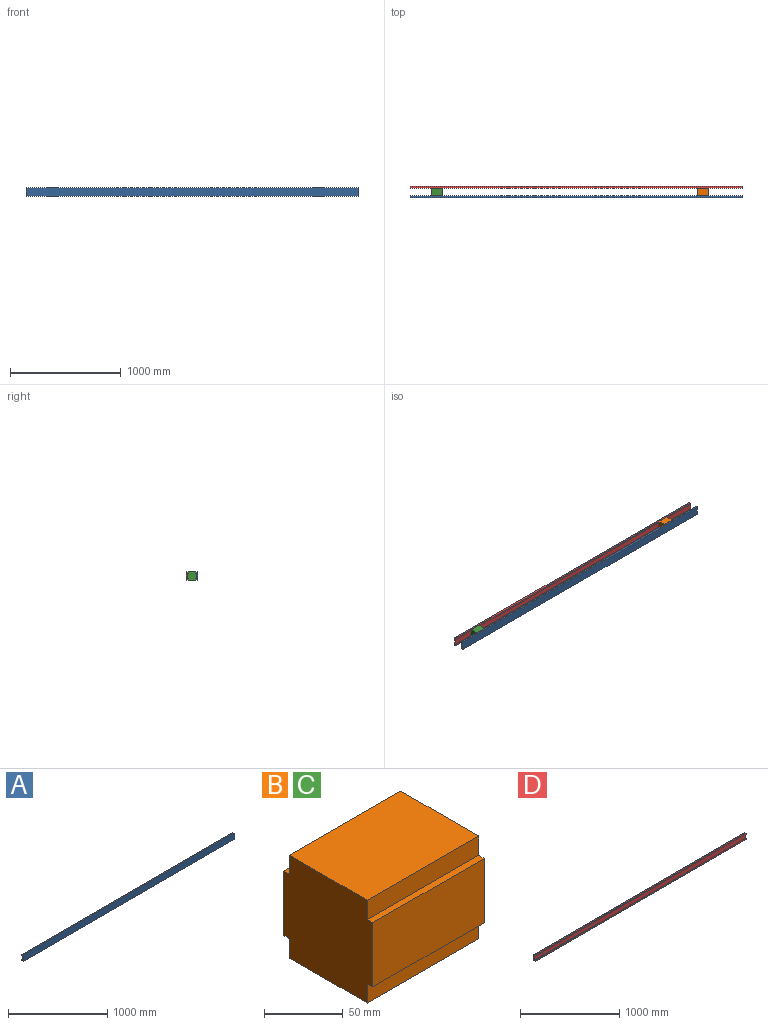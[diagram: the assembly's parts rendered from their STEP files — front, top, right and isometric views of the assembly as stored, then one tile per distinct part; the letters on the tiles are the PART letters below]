
ASSEMBLY  parts=4 mates=6
PART A: 10 faces, bbox 3000x15x80 mm
  f0: plane 3000x80mm, normal (0,-1,0), area 240000mm2, adj f1,f7,f8,f9
  f1: plane 3000x15mm, normal (0,0,-1), area 45000mm2, adj f0,f2,f8,f9
  f2: plane 3000x15mm, normal (0,1,0), area 45000mm2, adj f1,f3,f8,f9
  f3: plane 3000x5mm, normal (0,0,1), area 15000mm2, adj f2,f4,f8,f9
  f4: plane 3000x50mm, normal (0,1,0), area 150000mm2, adj f3,f5,f8,f9
  f5: plane 3000x5mm, normal (0,0,-1), area 15000mm2, adj f4,f6,f8,f9
  f6: plane 3000x15mm, normal (0,1,0), area 45000mm2, adj f5,f7,f8,f9
  f7: plane 3000x15mm, normal (0,0,1), area 45000mm2, adj f0,f6,f8,f9
  f8: plane 80x15mm, normal (1,0,0), area 950mm2, adj f0,f1,f2,f3,f4,f5,f6,f7
  f9: plane 80x15mm, normal (-1,0,0), area 950mm2, adj f0,f1,f2,f3,f4,f5,f6,f7
PART B: 14 faces, bbox 100x80x80 mm
  f0: plane 100x5mm, normal (0,0,1), area 500mm2, adj f1,f11,f12,f13
  f1: plane 100x15mm, normal (0,1,0), area 1500mm2, adj f0,f2,f12,f13
  f2: plane 100x70mm, normal (0,0,1), area 7000mm2, adj f1,f3,f12,f13
  f3: plane 100x15mm, normal (0,-1,0), area 1500mm2, adj f2,f4,f12,f13
  f4: plane 100x5mm, normal (0,0,1), area 500mm2, adj f3,f5,f12,f13
  f5: plane 100x50mm, normal (0,-1,0), area 5000mm2, adj f4,f6,f12,f13
  f6: plane 100x5mm, normal (0,0,-1), area 500mm2, adj f5,f7,f12,f13
  f7: plane 100x15mm, normal (0,-1,0), area 1500mm2, adj f6,f8,f12,f13
  f8: plane 100x70mm, normal (0,0,-1), area 7000mm2, adj f7,f9,f12,f13
  f9: plane 100x15mm, normal (0,1,0), area 1500mm2, adj f8,f10,f12,f13
  f10: plane 100x5mm, normal (0,0,-1), area 500mm2, adj f9,f11,f12,f13
  f11: plane 100x50mm, normal (0,1,0), area 5000mm2, adj f0,f10,f12,f13
  f12: plane 80x80mm, normal (1,0,0), area 6100mm2, adj f0,f1,f2,f3,f4,f5,f6,f7
  f13: plane 80x80mm, normal (-1,0,0), area 6100mm2, adj f0,f1,f2,f3,f4,f5,f6,f7
PART C: same geometry as B
PART D: 10 faces, bbox 3000x15x80 mm
  f0: plane 3000x15mm, normal (0,-1,0), area 45000mm2, adj f1,f7,f8,f9
  f1: plane 3000x15mm, normal (0,0,-1), area 45000mm2, adj f0,f2,f8,f9
  f2: plane 3000x80mm, normal (0,1,0), area 240000mm2, adj f1,f3,f8,f9
  f3: plane 3000x15mm, normal (0,0,1), area 45000mm2, adj f2,f4,f8,f9
  f4: plane 3000x15mm, normal (0,-1,0), area 45000mm2, adj f3,f5,f8,f9
  f5: plane 3000x5mm, normal (0,0,-1), area 15000mm2, adj f4,f6,f8,f9
  f6: plane 3000x50mm, normal (0,-1,0), area 150000mm2, adj f5,f7,f8,f9
  f7: plane 3000x5mm, normal (0,0,1), area 15000mm2, adj f0,f6,f8,f9
  f8: plane 80x15mm, normal (1,0,0), area 950mm2, adj f0,f1,f2,f3,f4,f5,f6,f7
  f9: plane 80x15mm, normal (-1,0,0), area 950mm2, adj f0,f1,f2,f3,f4,f5,f6,f7
PLACE A t=(-1500,-100,-80)mm
PLACE B t=(-355.96,-100,-80)mm
PLACE C t=(-2752.44,-100,-80)mm
PLACE D t=(-1500,-100,-80)mm
MATE parallel D.f2 <-> A.f0  axis (0,1,0) through (-3000,0,-40)mm
MATE slider B.f13 <-> A.f9  axis (-1,0,0) through (-405.96,-85,-15)mm
MATE planar D.f3 <-> A.f7  axis (0,0,1) through (-1500,-7.5,0)mm
MATE planar A.f9 <-> D.f9  axis (-1,0,0) through (-3000,-92.5,0)mm
MATE slider C.f13 <-> D.f9  axis (-1,0,0) through (-2802.44,-15,-15)mm
MATE slider B.f13 <-> D.f9  axis (-1,0,0) through (-405.96,-15,-15)mm
